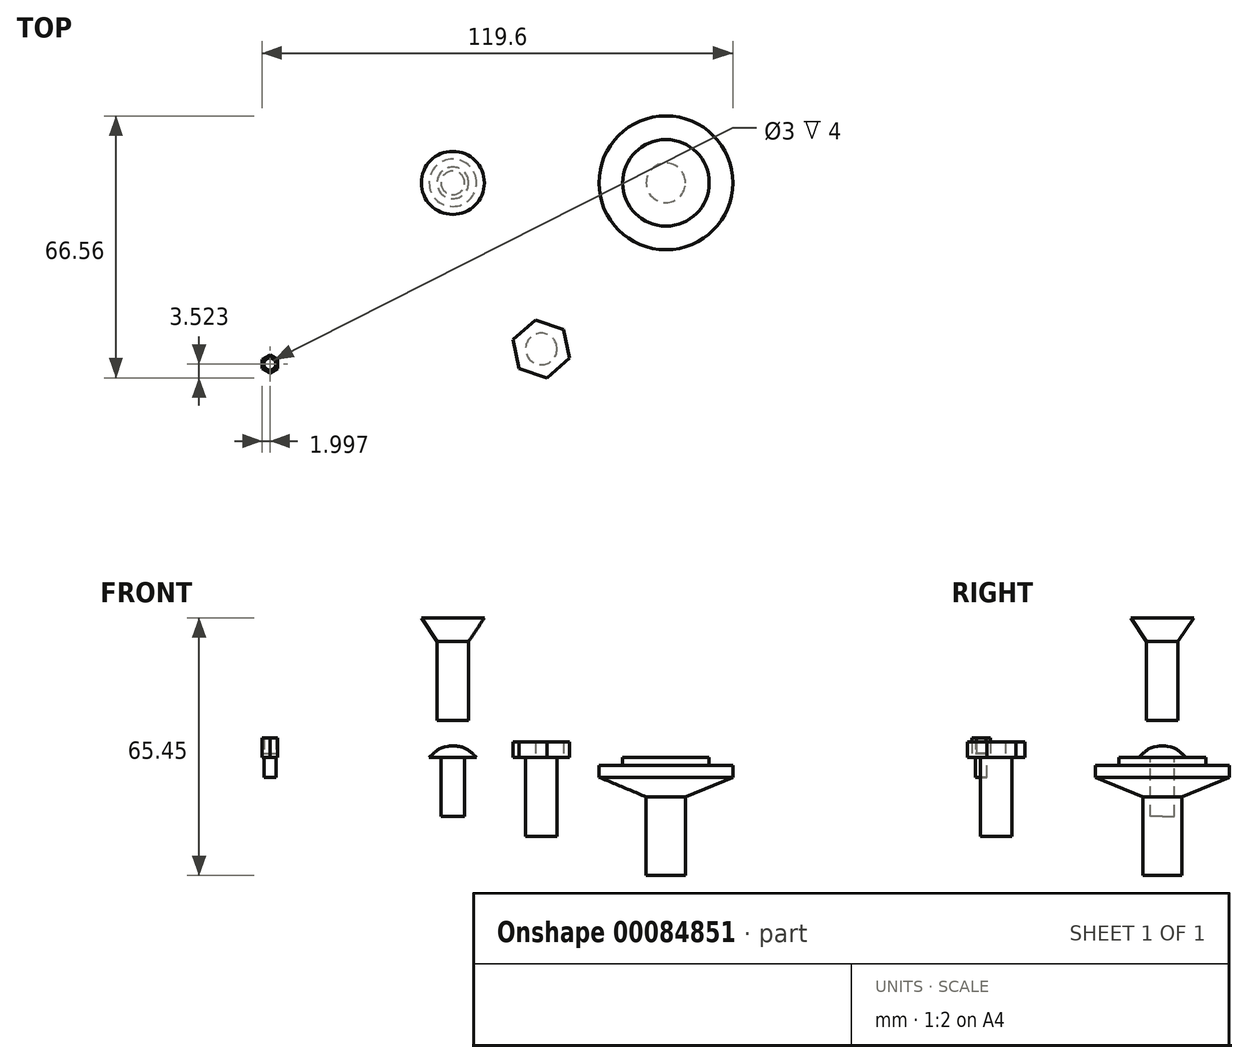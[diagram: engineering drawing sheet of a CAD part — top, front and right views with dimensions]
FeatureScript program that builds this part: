
annotation { "Feature Type Name" : "Feature", "Feature Type Description" : "" }
export const myFeature = defineFeature(function(context is Context, id is Id, definition is map)
    precondition{}
    {
        {
            var Q0;
            Q0=qCreatedBy(makeId("Front.planeOp"),FACE);
            var sketch = newSketch(context, id + "F0", { "sketchPlane" : qUnion([Q0])});
            skLineSegment(sketch, "E0", {"start": v(0, 3) * mm, "end": v(0, 0) * mm});
            skLineSegment(sketch, "E1", {"start": v(0, 0) * mm, "end": v(6, 0) * mm});
            skFitSpline(sketch, "E2", {"points": [v(6, 0) * mm, v(3.2, 2.3) * mm, v(0, 3) * mm], "startDerivative": vector(-5.16, 5.28) * mm, "endDerivative": vector(-6.85, 0.68) * mm});
            skLineSegment(sketch, "E3", {"start": v(0, 4.9) * mm, "end": v(0, -5.28) * mm, "construction": true});
            skSolve(sketch);
        }
        {
            var Q0;
            Q0=qSketchRegion(id+"F0",true);
            var Q1;
            Q1=sQuery(id+"F0.wireOp",EDGE,"E3");
            revolve(context, id + "F1", {"entities" : qUnion([Q0]), "axis" : qUnion([Q1]), "revolveType" : RevolveType.FULL});
        }
        {
            var Q0;
            Q0=makeQuery(id+"F1.opRevolve","SWEPT_FACE",FACE,{"disambiguationData":[OSD([sQuery(id+"F0.wireOp",EDGE,"E1")])]});
            var sketch = newSketch(context, id + "F2", { "sketchPlane" : qUnion([Q0])});
            skCircle(sketch, "E4", {"center": v(0, 0) * mm, "radius": 3 * mm});
            skSolve(sketch);
        }
        {
            var Q0;
            Q0=qSketchRegion(id+"F2",true);
            extrude(context, id + "F3", {"entities" : qUnion([Q0]), "operationType" : NewBodyOperationType.ADD, "depth" : 15 * mm});
        }
        {
            var Q0;
            Q0=qCreatedBy(makeId("Front.planeOp"),FACE);
            var sketch = newSketch(context, id + "F4", { "sketchPlane" : qUnion([Q0])});
            skLineSegment(sketch, "E5", {"start": v(0, 35.45) * mm, "end": v(0, 9.45) * mm});
            skLineSegment(sketch, "E6", {"start": v(0, 9.45) * mm, "end": v(4, 9.45) * mm});
            skLineSegment(sketch, "E7", {"start": v(4, 9.45) * mm, "end": v(4, 29.45) * mm});
            skLineSegment(sketch, "E8", {"start": v(4, 29.45) * mm, "end": v(8, 35.45) * mm});
            skLineSegment(sketch, "E9", {"start": v(8, 35.45) * mm, "end": v(0, 35.45) * mm});
            skSolve(sketch);
        }
        {
            var Q0;
            Q0=qSketchRegion(id+"F4",true);
            var Q1;
            Q1=sQuery(id+"F4.wireOp",EDGE,"E5");
            revolve(context, id + "F5", {"entities" : qUnion([Q0]), "axis" : qUnion([Q1]), "revolveType" : RevolveType.FULL});
        }
        {
            var Q0;
            Q0=qCreatedBy(makeId("Top.planeOp"),FACE);
            var sketch = newSketch(context, id + "F6", { "sketchPlane" : qUnion([Q0])});
            skCircle(sketch, "E10", {"center": v(22.48, -42.2) * mm, "radius": 4 * mm});
            skSolve(sketch);
        }
        {
            var Q0;
            Q0=qSketchRegion(id+"F6",true);
            extrude(context, id + "F7", {"entities" : qUnion([Q0]), "oppositeDirection" : true, "depth" : 20 * mm});
        }
        {
            var Q0;
            Q0=makeQuery(id+"F7.opExtrude","CAP_FACE",FACE,{"disambiguationData":[OSD([sQuery(id+"F6.wireOp",EDGE,"E10")])],"isStart":true});
            var sketch = newSketch(context, id + "F8", { "sketchPlane" : qUnion([Q0])});
            skCircle(sketch, "E11.cCircle", {"center": v(22.48, -42.2) * mm, "radius": 6.5 * mm, "construction": true});
            skLineSegment(sketch, "E11.0", {"start": v(15.35, -39.85) * mm, "end": v(20.96, -34.86) * mm});
            skLineSegment(sketch, "E11.1", {"start": v(20.96, -34.86) * mm, "end": v(28.09, -37.22) * mm});
            skLineSegment(sketch, "E11.2", {"start": v(28.09, -37.22) * mm, "end": v(29.6, -44.57) * mm});
            skLineSegment(sketch, "E11.3", {"start": v(29.6, -44.57) * mm, "end": v(24, -49.56) * mm});
            skLineSegment(sketch, "E11.4", {"start": v(24, -49.56) * mm, "end": v(16.87, -47.2) * mm});
            skLineSegment(sketch, "E11.5", {"start": v(16.87, -47.2) * mm, "end": v(15.35, -39.85) * mm});
            skPoint(sketch, "E11.0.midPoint", {"position": v(18.16, -37.35) * mm});
            skSolve(sketch);
        }
        {
            var Q0;
            Q0=qSketchRegion(id+"F8",true);
            extrude(context, id + "F9", {"entities" : qUnion([Q0]), "operationType" : NewBodyOperationType.ADD, "depth" : 4 * mm});
        }
        {
            var Q0;
            Q0=qCreatedBy(makeId("Top.planeOp"),FACE);
            var sketch = newSketch(context, id + "F10", { "sketchPlane" : qUnion([Q0])});
            skCircle(sketch, "E12.cCircle", {"center": v(-46.46, -46.04) * mm, "radius": 2 * mm, "construction": true});
            skLineSegment(sketch, "E12.0", {"start": v(-44.46, -44.88) * mm, "end": v(-44.46, -47.2) * mm});
            skLineSegment(sketch, "E12.1", {"start": v(-44.46, -47.2) * mm, "end": v(-46.46, -48.35) * mm});
            skLineSegment(sketch, "E12.2", {"start": v(-46.46, -48.35) * mm, "end": v(-48.46, -47.2) * mm});
            skLineSegment(sketch, "E12.3", {"start": v(-48.46, -47.2) * mm, "end": v(-48.46, -44.88) * mm});
            skLineSegment(sketch, "E12.4", {"start": v(-48.46, -44.88) * mm, "end": v(-46.46, -43.73) * mm});
            skLineSegment(sketch, "E12.5", {"start": v(-46.46, -43.73) * mm, "end": v(-44.46, -44.88) * mm});
            skPoint(sketch, "E12.0.midPoint", {"position": v(-44.46, -46.04) * mm});
            skSolve(sketch);
        }
        {
            var Q0;
            Q0=qSketchRegion(id+"F10",true);
            extrude(context, id + "F11", {"entities" : qUnion([Q0]), "depth" : 5 * mm});
        }
        {
            var Q0;
            Q0=makeQuery(id+"F11.opExtrude","CAP_FACE",FACE,{"disambiguationData":[OSD([sQuery(id+"F10.wireOp",EDGE,"E12.0"),sQuery(id+"F10.wireOp",EDGE,"E12.1"),sQuery(id+"F10.wireOp",EDGE,"E12.2"),sQuery(id+"F10.wireOp",EDGE,"E12.3"),sQuery(id+"F10.wireOp",EDGE,"E12.4"),sQuery(id+"F10.wireOp",EDGE,"E12.5")])],"isStart":true});
            var sketch = newSketch(context, id + "F12", { "sketchPlane" : qUnion([Q0])});
            skCircle(sketch, "E13", {"center": v(-46.46, 46.04) * mm, "radius": 1.5 * mm});
            skLineSegment(sketch, "E14", {"start": v(-46.46, 43.73) * mm, "end": v(-46.46, 48.35) * mm, "construction": true});
            skLineSegment(sketch, "E15", {"start": v(-48.46, 47.2) * mm, "end": v(-44.46, 44.88) * mm, "construction": true});
            skSolve(sketch);
        }
        {
            var Q0;
            Q0=qSketchRegion(id+"F12",true);
            extrude(context, id + "F13", {"entities" : qUnion([Q0]), "operationType" : NewBodyOperationType.REMOVE, "oppositeDirection" : true, "depth" : 6 * mm});
        }
        {
            var Q0;
            Q0=qSketchRegion(id+"F12",true);
            extrude(context, id + "F14", {"entities" : qUnion([Q0]), "operationType" : NewBodyOperationType.ADD, "depth" : 5 * mm, "hasSecondDirection" : true, "secondDirectionOppositeDirection" : true, "secondDirectionDepth" : 1 * mm});
        }
        {
            var Q0;
            Q0=qCreatedBy(makeId("Front.planeOp"),FACE);
            var sketch = newSketch(context, id + "F15", { "sketchPlane" : qUnion([Q0])});
            skLineSegment(sketch, "E16", {"start": v(54.14, 0) * mm, "end": v(65.14, 0) * mm});
            skLineSegment(sketch, "E17", {"start": v(65.14, 0) * mm, "end": v(65.14, -2) * mm});
            skLineSegment(sketch, "E18", {"start": v(65.14, -2) * mm, "end": v(71.14, -2) * mm});
            skLineSegment(sketch, "E19", {"start": v(71.14, -2) * mm, "end": v(71.14, -5) * mm});
            skLineSegment(sketch, "E20", {"start": v(71.14, -5) * mm, "end": v(59.14, -10) * mm});
            skLineSegment(sketch, "E21", {"start": v(59.14, -10) * mm, "end": v(59.14, -30) * mm});
            skLineSegment(sketch, "E22", {"start": v(59.14, -30) * mm, "end": v(54.14, -30) * mm});
            skLineSegment(sketch, "E23", {"start": v(54.14, -30) * mm, "end": v(54.14, 0) * mm});
            skSolve(sketch);
        }
        {
            var Q0;
            Q0=qSketchRegion(id+"F15",true);
            var Q1;
            Q1=sQuery(id+"F15.wireOp",EDGE,"E23");
            revolve(context, id + "F16", {"entities" : qUnion([Q0]), "axis" : qUnion([Q1]), "revolveType" : RevolveType.FULL});
        }
    });
